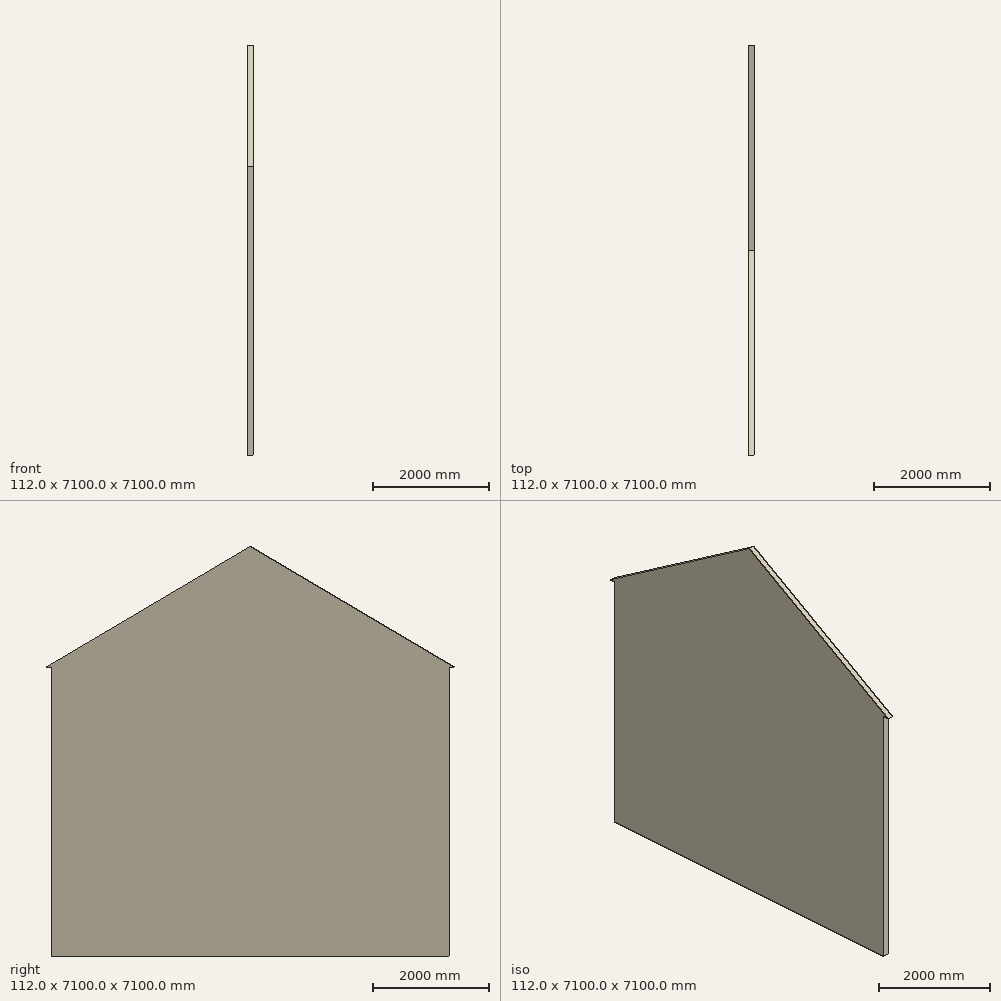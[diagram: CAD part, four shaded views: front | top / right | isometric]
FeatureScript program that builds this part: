
annotation { "Feature Type Name" : "Feature", "Feature Type Description" : "" }
export const myFeature = defineFeature(function(context is Context, id is Id, definition is map)
    precondition{}
    {
        {
            var Q0;
            Q0=qCreatedBy(makeId("Right.planeOp"),FACE);
            var sketch = newSketch(context, id + "F0", { "sketchPlane" : qUnion([Q0])});
            skLineSegment(sketch, "E0.bottom", {"start": v(3436.36, -2713.57) * mm, "end": v(-3439.64, -2713.57) * mm});
            skLineSegment(sketch, "E1", {"start": v(3548.36, 2286.43) * mm, "end": v(-1.64, 4386.43) * mm});
            skLineSegment(sketch, "E2", {"start": v(-3551.64, 2286.43) * mm, "end": v(-1.64, 4386.43) * mm});
            skLineSegment(sketch, "E3", {"start": v(-3439.64, -2713.57) * mm, "end": v(-3439.64, 2286.43) * mm});
            skLineSegment(sketch, "E4", {"start": v(3436.36, 2286.43) * mm, "end": v(3436.36, -2713.57) * mm});
            skLineSegment(sketch, "E5", {"start": v(-3551.64, 2286.43) * mm, "end": v(-3439.64, 2286.43) * mm});
            skLineSegment(sketch, "E6", {"start": v(3548.36, 2286.43) * mm, "end": v(3436.36, 2286.43) * mm});
            skSolve(sketch);
        }
        {
            var Q0;
            Q0 = qSketchRegion(id + "F0", true);
            extrude(context, id + "F1", {"entities" : qUnion([Q0]), "depth" : 112 * mm, "offsetDistance" : 25 * mm});
        }
    });
